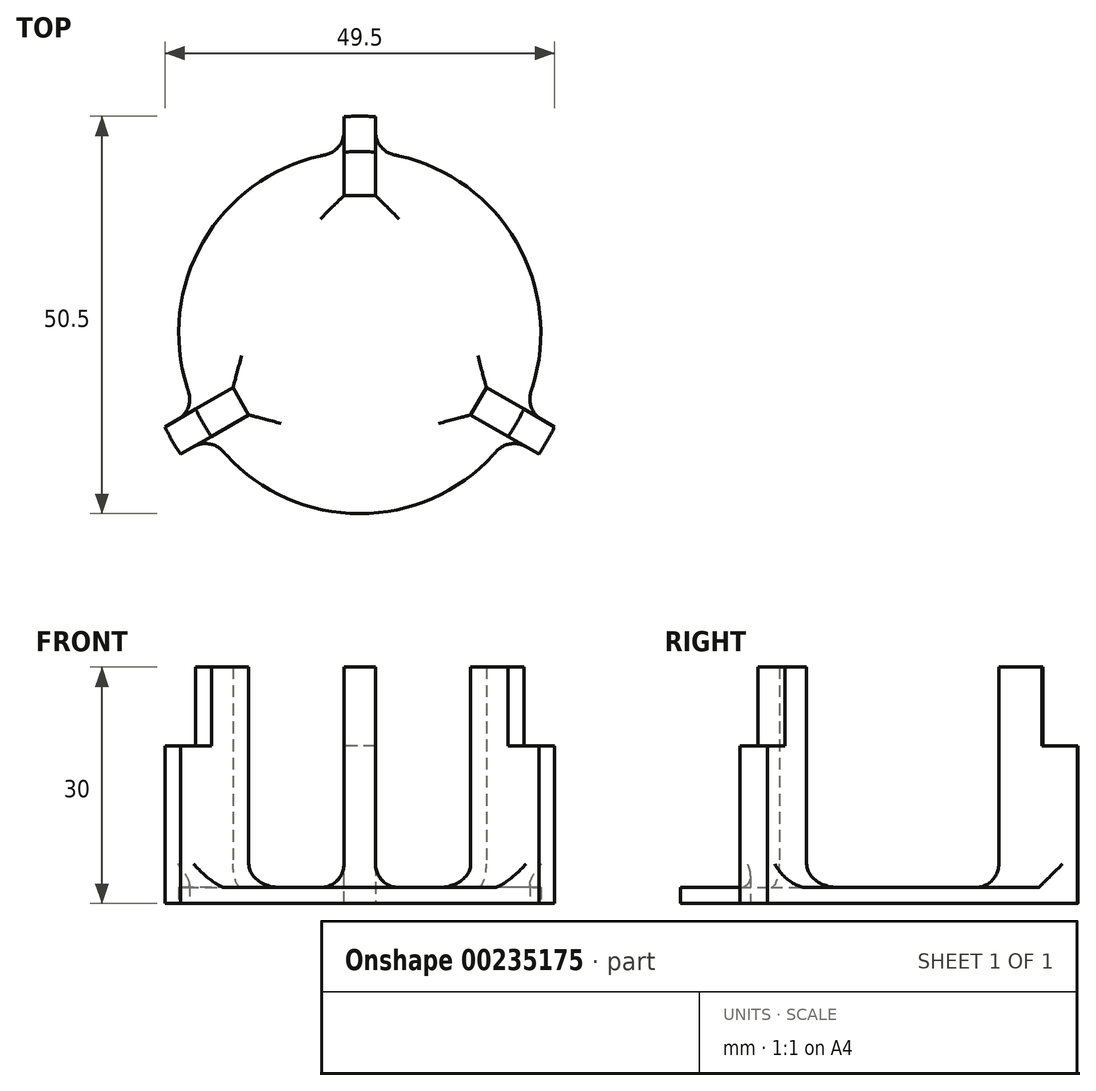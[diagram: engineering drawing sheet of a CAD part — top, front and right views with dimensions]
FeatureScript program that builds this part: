
annotation { "Feature Type Name" : "Feature", "Feature Type Description" : "" }
export const myFeature = defineFeature(function(context is Context, id is Id, definition is map)
    precondition{}
    {
        {
            var Q0;
            Q0=qCreatedBy(makeId("Top.planeOp"),FACE);
            var sketch = newSketch(context, id + "F3", { "sketchPlane" : qUnion([Q0])});
            skCircle(sketch, "E0", {"center": v(0, 0) * mm, "radius": 25 * mm});
            skSolve(sketch);
        }
        {
            var Q0;
            Q0=qCreatedBy(makeId("Top.planeOp"),FACE);
            var sketch = newSketch(context, id + "F4", { "sketchPlane" : qUnion([Q0])});
            skCircle(sketch, "E1", {"center": v(0, 0) * mm, "radius": 27.5 * mm});
            skLineSegment(sketch, "E2.bottom", {"start": v(-2, 27.43) * mm, "end": v(2, 27.43) * mm});
            skLineSegment(sketch, "E2.top", {"start": v(-2, 17.43) * mm, "end": v(2, 17.43) * mm});
            skLineSegment(sketch, "E2.left", {"start": v(-2, 27.43) * mm, "end": v(-2, 17.43) * mm});
            skLineSegment(sketch, "E2.right", {"start": v(2, 27.43) * mm, "end": v(2, 17.43) * mm});
            skLineSegment(sketch, "E3", {"start": v(0, 24.43) * mm, "end": v(2, 24.43) * mm});
            skCircle(sketch, "E4", {"center": v(0, 0) * mm, "radius": 23 * mm});
            skSolve(sketch);
        }
        {
            var Q0;
            {var subQ0=sQuery(id+"F4.wireOp",EDGE,"E2.top");Q0=makeQuery(id+"F4.imprint","IMPRINT",FACE,{"disambiguationData":[TD([[makeQuery(id+"F4.imprint","IMPRINT",EDGE,{"derivedFrom":subQ0}),1.0]])]});}
            var Q1;
            {var subQ0=sQuery(id+"F4.wireOp",EDGE,"E3");var subQ1=sQuery(id+"F4.wireOp",EDGE,"E2.left");var subQ2=makeQuery(id+"F4.imprint","INTERSECT",VERTEX,{"derivedFrom":[subQ1,subQ0]});Q1=makeQuery(id+"F4.imprint","IMPRINT",FACE,{"disambiguationData":[TD([[makeQuery(id+"F4.imprint","IMPRINT",EDGE,{"disambiguationData":[TD([[subQ2,-1.0]])],"derivedFrom":subQ1}),1.0]])]});}
            extrude(context, id + "F5", {"entities" : qUnion([Q0, Q1]), "depth" : 30 * mm});
        }
        {
            var Q0;
            {var subQ0=sQuery(id+"F4.wireOp",EDGE,"E2.bottom");Q0=makeQuery(id+"F4.imprint","IMPRINT",FACE,{"disambiguationData":[TD([[makeQuery(id+"F4.imprint","IMPRINT",EDGE,{"derivedFrom":subQ0}),-1.0]])]});}
            var Q1;
            {var subQ0=sQuery(id+"F4.wireOp",EDGE,"E2.bottom");Q1=makeQuery(id+"F4.imprint","IMPRINT",FACE,{"disambiguationData":[TD([[makeQuery(id+"F4.imprint","IMPRINT",EDGE,{"derivedFrom":subQ0}),1.0]])]});}
            extrude(context, id + "F6", {"entities" : qUnion([Q0, Q1]), "operationType" : NewBodyOperationType.ADD, "depth" : 20 * mm});
        }
        {
            var Q0;
            Q0=makeQuery(id+"F5.opExtrude","SWEPT_BODY",BODY,{"disambiguationData":[OSD([sQuery(id+"F4.wireOp",EDGE,"E2.top"),sQuery(id+"F4.wireOp",EDGE,"E2.left"),sQuery(id+"F4.wireOp",EDGE,"E2.right"),sQuery(id+"F4.wireOp",EDGE,"E3")])]});
            var Q1;
            Q1=sQuery(id+"F3.wireOp",EDGE,"E0");
            circularPattern(context, id + "F0", {"entities" : qUnion([Q0]), "axis" : qUnion([Q1]), "angle" : 360 * degree, "instanceCount" : 3, "equalSpace" : true});
        }
        {
            var Q0;
            {var subQ0=sQuery(id+"F4.wireOp",EDGE,"E2.top");Q0=makeQuery(id+"F4.imprint","IMPRINT",FACE,{"disambiguationData":[TD([[makeQuery(id+"F4.imprint","IMPRINT",EDGE,{"derivedFrom":subQ0}),1.0]])]});}
            var Q1;
            {var subQ0=sQuery(id+"F4.wireOp",EDGE,"E2.top");Q1=makeQuery(id+"F4.imprint","IMPRINT",FACE,{"disambiguationData":[TD([[makeQuery(id+"F4.imprint","IMPRINT",EDGE,{"derivedFrom":subQ0}),-1.0]])]});}
            extrude(context, id + "F1", {"entities" : qUnion([Q0, Q1]), "operationType" : NewBodyOperationType.ADD, "depth" : 2 * mm});
        }
        {
            var Q0;
            {var subQ0=sQuery(id+"F4.wireOp",EDGE,"E2.left");Q0=makeQuery(id+"F1.boolean.opBoolean","INTERSECT",EDGE,{"derivedFrom":[makeQuery(id+"F6.boolean.opBoolean","MERGE",FACE,{"derivedFrom":[makeQuery(id+"F5.opExtrude","SWEPT_FACE",FACE,{"disambiguationData":[OSD([subQ0])]}),makeQuery(id+"F6.opExtrude","SWEPT_FACE",FACE,{"disambiguationData":[OSD([subQ0])]})]}),makeQuery(id+"F1.opExtrude","CAP_FACE",FACE,{"disambiguationData":[OSD([sQuery(id+"F4.wireOp",EDGE,"E4")])],"isStart":false})]});}
            var Q1;
            Q1=makeQuery(id+"F1.boolean.opBoolean","INTERSECT",EDGE,{"derivedFrom":[makeQuery(id+"F5.opExtrude","SWEPT_FACE",FACE,{"disambiguationData":[OSD([sQuery(id+"F4.wireOp",EDGE,"E2.top")])]}),makeQuery(id+"F1.opExtrude","CAP_FACE",FACE,{"disambiguationData":[OSD([sQuery(id+"F4.wireOp",EDGE,"E4")])],"isStart":false})]});
            var Q2;
            {var subQ0=sQuery(id+"F4.wireOp",EDGE,"E2.right");Q2=makeQuery(id+"F1.boolean.opBoolean","INTERSECT",EDGE,{"derivedFrom":[makeQuery(id+"F6.boolean.opBoolean","MERGE",FACE,{"derivedFrom":[makeQuery(id+"F5.opExtrude","SWEPT_FACE",FACE,{"disambiguationData":[OSD([subQ0])]}),makeQuery(id+"F6.opExtrude","SWEPT_FACE",FACE,{"disambiguationData":[OSD([subQ0])]})]}),makeQuery(id+"F1.opExtrude","CAP_FACE",FACE,{"disambiguationData":[OSD([sQuery(id+"F4.wireOp",EDGE,"E4")])],"isStart":false})]});}
            var Q3;
            {var subQ0=sQuery(id+"F4.wireOp",EDGE,"E2.right");Q3=makeQuery(id+"F1.boolean.opBoolean","INTERSECT",EDGE,{"derivedFrom":[makeQuery(id+"F0.opPattern","COPY",FACE,{"derivedFrom":makeQuery(id+"F6.boolean.opBoolean","MERGE",FACE,{"derivedFrom":[makeQuery(id+"F5.opExtrude","SWEPT_FACE",FACE,{"disambiguationData":[OSD([subQ0])]}),makeQuery(id+"F6.opExtrude","SWEPT_FACE",FACE,{"disambiguationData":[OSD([subQ0])]})]}),"instanceName":"2"}),makeQuery(id+"F1.opExtrude","CAP_FACE",FACE,{"disambiguationData":[OSD([sQuery(id+"F4.wireOp",EDGE,"E4")])],"isStart":false})]});}
            var Q4;
            Q4=makeQuery(id+"F1.boolean.opBoolean","INTERSECT",EDGE,{"derivedFrom":[makeQuery(id+"F0.opPattern","COPY",FACE,{"derivedFrom":makeQuery(id+"F5.opExtrude","SWEPT_FACE",FACE,{"disambiguationData":[OSD([sQuery(id+"F4.wireOp",EDGE,"E2.top")])]}),"instanceName":"2"}),makeQuery(id+"F1.opExtrude","CAP_FACE",FACE,{"disambiguationData":[OSD([sQuery(id+"F4.wireOp",EDGE,"E4")])],"isStart":false})]});
            var Q5;
            {var subQ0=sQuery(id+"F4.wireOp",EDGE,"E2.left");Q5=makeQuery(id+"F1.boolean.opBoolean","INTERSECT",EDGE,{"derivedFrom":[makeQuery(id+"F0.opPattern","COPY",FACE,{"derivedFrom":makeQuery(id+"F6.boolean.opBoolean","MERGE",FACE,{"derivedFrom":[makeQuery(id+"F5.opExtrude","SWEPT_FACE",FACE,{"disambiguationData":[OSD([subQ0])]}),makeQuery(id+"F6.opExtrude","SWEPT_FACE",FACE,{"disambiguationData":[OSD([subQ0])]})]}),"instanceName":"2"}),makeQuery(id+"F1.opExtrude","CAP_FACE",FACE,{"disambiguationData":[OSD([sQuery(id+"F4.wireOp",EDGE,"E4")])],"isStart":false})]});}
            var Q6;
            {var subQ0=sQuery(id+"F4.wireOp",EDGE,"E2.right");Q6=makeQuery(id+"F1.boolean.opBoolean","INTERSECT",EDGE,{"derivedFrom":[makeQuery(id+"F0.opPattern","COPY",FACE,{"derivedFrom":makeQuery(id+"F6.boolean.opBoolean","MERGE",FACE,{"derivedFrom":[makeQuery(id+"F5.opExtrude","SWEPT_FACE",FACE,{"disambiguationData":[OSD([subQ0])]}),makeQuery(id+"F6.opExtrude","SWEPT_FACE",FACE,{"disambiguationData":[OSD([subQ0])]})]}),"instanceName":"1"}),makeQuery(id+"F1.opExtrude","CAP_FACE",FACE,{"disambiguationData":[OSD([sQuery(id+"F4.wireOp",EDGE,"E4")])],"isStart":false})]});}
            var Q7;
            Q7=makeQuery(id+"F1.boolean.opBoolean","INTERSECT",EDGE,{"derivedFrom":[makeQuery(id+"F0.opPattern","COPY",FACE,{"derivedFrom":makeQuery(id+"F5.opExtrude","SWEPT_FACE",FACE,{"disambiguationData":[OSD([sQuery(id+"F4.wireOp",EDGE,"E2.top")])]}),"instanceName":"1"}),makeQuery(id+"F1.opExtrude","CAP_FACE",FACE,{"disambiguationData":[OSD([sQuery(id+"F4.wireOp",EDGE,"E4")])],"isStart":false})]});
            var Q8;
            {var subQ0=sQuery(id+"F4.wireOp",EDGE,"E2.left");Q8=makeQuery(id+"F1.boolean.opBoolean","INTERSECT",EDGE,{"derivedFrom":[makeQuery(id+"F0.opPattern","COPY",FACE,{"derivedFrom":makeQuery(id+"F6.boolean.opBoolean","MERGE",FACE,{"derivedFrom":[makeQuery(id+"F5.opExtrude","SWEPT_FACE",FACE,{"disambiguationData":[OSD([subQ0])]}),makeQuery(id+"F6.opExtrude","SWEPT_FACE",FACE,{"disambiguationData":[OSD([subQ0])]})]}),"instanceName":"1"}),makeQuery(id+"F1.opExtrude","CAP_FACE",FACE,{"disambiguationData":[OSD([sQuery(id+"F4.wireOp",EDGE,"E4")])],"isStart":false})]});}
            var Q9;
            {var subQ0=sQuery(id+"F4.wireOp",EDGE,"E2.left");Q9=makeQuery(id+"F1.boolean.opBoolean","INTERSECT",EDGE,{"derivedFrom":[makeQuery(id+"F6.boolean.opBoolean","MERGE",FACE,{"derivedFrom":[makeQuery(id+"F5.opExtrude","SWEPT_FACE",FACE,{"disambiguationData":[OSD([subQ0])]}),makeQuery(id+"F6.opExtrude","SWEPT_FACE",FACE,{"disambiguationData":[OSD([subQ0])]})]}),makeQuery(id+"F1.opExtrude","SWEPT_FACE",FACE,{"disambiguationData":[OSD([sQuery(id+"F4.wireOp",EDGE,"E4")])]})]});}
            var Q10;
            {var subQ0=sQuery(id+"F4.wireOp",EDGE,"E2.right");Q10=makeQuery(id+"F1.boolean.opBoolean","INTERSECT",EDGE,{"derivedFrom":[makeQuery(id+"F0.opPattern","COPY",FACE,{"derivedFrom":makeQuery(id+"F6.boolean.opBoolean","MERGE",FACE,{"derivedFrom":[makeQuery(id+"F5.opExtrude","SWEPT_FACE",FACE,{"disambiguationData":[OSD([subQ0])]}),makeQuery(id+"F6.opExtrude","SWEPT_FACE",FACE,{"disambiguationData":[OSD([subQ0])]})]}),"instanceName":"1"}),makeQuery(id+"F1.opExtrude","SWEPT_FACE",FACE,{"disambiguationData":[OSD([sQuery(id+"F4.wireOp",EDGE,"E4")])]})]});}
            var Q11;
            {var subQ0=sQuery(id+"F4.wireOp",EDGE,"E2.right");Q11=makeQuery(id+"F1.boolean.opBoolean","INTERSECT",EDGE,{"derivedFrom":[makeQuery(id+"F6.boolean.opBoolean","MERGE",FACE,{"derivedFrom":[makeQuery(id+"F5.opExtrude","SWEPT_FACE",FACE,{"disambiguationData":[OSD([subQ0])]}),makeQuery(id+"F6.opExtrude","SWEPT_FACE",FACE,{"disambiguationData":[OSD([subQ0])]})]}),makeQuery(id+"F1.opExtrude","SWEPT_FACE",FACE,{"disambiguationData":[OSD([sQuery(id+"F4.wireOp",EDGE,"E4")])]})]});}
            var Q12;
            {var subQ0=sQuery(id+"F4.wireOp",EDGE,"E2.left");Q12=makeQuery(id+"F1.boolean.opBoolean","INTERSECT",EDGE,{"derivedFrom":[makeQuery(id+"F0.opPattern","COPY",FACE,{"derivedFrom":makeQuery(id+"F6.boolean.opBoolean","MERGE",FACE,{"derivedFrom":[makeQuery(id+"F5.opExtrude","SWEPT_FACE",FACE,{"disambiguationData":[OSD([subQ0])]}),makeQuery(id+"F6.opExtrude","SWEPT_FACE",FACE,{"disambiguationData":[OSD([subQ0])]})]}),"instanceName":"2"}),makeQuery(id+"F1.opExtrude","SWEPT_FACE",FACE,{"disambiguationData":[OSD([sQuery(id+"F4.wireOp",EDGE,"E4")])]})]});}
            var Q13;
            {var subQ0=sQuery(id+"F4.wireOp",EDGE,"E2.right");Q13=makeQuery(id+"F1.boolean.opBoolean","INTERSECT",EDGE,{"derivedFrom":[makeQuery(id+"F0.opPattern","COPY",FACE,{"derivedFrom":makeQuery(id+"F6.boolean.opBoolean","MERGE",FACE,{"derivedFrom":[makeQuery(id+"F5.opExtrude","SWEPT_FACE",FACE,{"disambiguationData":[OSD([subQ0])]}),makeQuery(id+"F6.opExtrude","SWEPT_FACE",FACE,{"disambiguationData":[OSD([subQ0])]})]}),"instanceName":"2"}),makeQuery(id+"F1.opExtrude","SWEPT_FACE",FACE,{"disambiguationData":[OSD([sQuery(id+"F4.wireOp",EDGE,"E4")])]})]});}
            var Q14;
            {var subQ0=sQuery(id+"F4.wireOp",EDGE,"E2.left");Q14=makeQuery(id+"F1.boolean.opBoolean","INTERSECT",EDGE,{"derivedFrom":[makeQuery(id+"F0.opPattern","COPY",FACE,{"derivedFrom":makeQuery(id+"F6.boolean.opBoolean","MERGE",FACE,{"derivedFrom":[makeQuery(id+"F5.opExtrude","SWEPT_FACE",FACE,{"disambiguationData":[OSD([subQ0])]}),makeQuery(id+"F6.opExtrude","SWEPT_FACE",FACE,{"disambiguationData":[OSD([subQ0])]})]}),"instanceName":"1"}),makeQuery(id+"F1.opExtrude","SWEPT_FACE",FACE,{"disambiguationData":[OSD([sQuery(id+"F4.wireOp",EDGE,"E4")])]})]});}
            fillet(context, id + "F2", {"entities" : qUnion([Q0, Q1, Q2, Q3, Q4, Q5, Q6, Q7, Q8, Q9, Q10, Q11, Q12, Q13, Q14]), "radius" : 3 * mm, "tangentPropagation" : true, "allowEdgeOverflow" : false});
        }
    });
